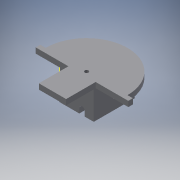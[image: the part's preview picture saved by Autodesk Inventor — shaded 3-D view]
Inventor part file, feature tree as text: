
AUTODESK INVENTOR PART (.ipt)
format: ipt  version: 2016 (Build 200138000, 138)  size: 617,472 bytes
history: native  units: in
note: dims shown in document units (in); Inventor stores cm internally (conversion verified against a paired STEP export)
features: reference x42, extrude x34, sketch x34, plane x6, projected_geometry x5
ambient origin geometry x8: Origin, YZ Plane, XZ Plane, XY Plane, X Axis, Y Axis, Z Axis, Center Point
bodies: Solid1 (feature_tree)
feature tree (121):
  extrude  "Extrusion1"  Depth=3.0in
  extrude  "Extrusion2"  Depth=0.1969in
  extrude  "Extrusion3"  Depth=1.0827in
  extrude  "Extrusion5"  Depth=1.0in TaperAngle=0.0deg
  plane  "Work Plane1"
  extrude  "Extrusion6"  Depth=0.0098in
  extrude  "Extrusion9"  Depth=0.0787in
  extrude  "Extrusion14"  Depth=0.1575in
  extrude  "Extrusion15"  Depth=1.25in
  plane  "Work Plane2"
  extrude  "Extrusion16"  Depth=0.1575in
  extrude  "Extrusion17"  Depth=0.1181in TaperAngle=0.0deg
  extrude  "Extrusion18"  Depth=0.1969in
  plane  "Work Plane3"
  extrude  "Extrusion20"  Depth=0.1969in TaperAngle=0.0deg
  extrude  "Extrusion21"  Depth=0.1181in TaperAngle=0.0deg
  plane  "Work Plane4"
  plane  "Work Plane5"
  extrude  "Extrusion23"  Depth=0.1181in
  extrude  "Extrusion24"  Depth=0.1969in TaperAngle=0.0deg
  plane  "Work Plane6"
  extrude  "Extrusion25"  Depth=0.35in
  extrude  "Extrusion26"  Depth=0.2in
  extrude  "Extrusion27"  Depth=0.1969in TaperAngle=0.0deg
  extrude  "Extrusion28"  Depth=1.5in
  extrude  "Extrusion29"  Depth=0.7in
  extrude  "Extrusion30"  Depth=0.1181in TaperAngle=0.0deg
  extrude  "Extrusion31"  Depth=1.0in
  extrude  "Extrusion34"  Depth=0.5in
  sketch  "Sketch36"  dims[d105=0.1181in d106=0.5in]
  extrude  "Extrusion35"  Depth=0.5in
  extrude  "Extrusion36"  Depth=0.0197in
  extrude  "Extrusion37"  Depth=0.325in
  extrude  "Extrusion38"  Depth=0.1969in
  extrude  "Extrusion39"  Depth=0.1181in
  sketch  "Sketch41"  dims[d117=0.1969in d118=0.1181in]
  extrude  "Extrusion41"  Depth=0.1969in TaperAngle=0.0deg
  extrude  "Extrusion42"  Depth=1.0in TaperAngle=0.0deg
  extrude  "Extrusion43"  Depth=0.5in
  extrude  "Extrusion44"  Depth=0.0039in
  extrude  "Extrusion45"  Depth=0.0984in
  extrude  "Extrusion46"  Depth=0.3937in
  sketch  "Sketch1"  dims[d0=4.5in d1=3.0in]
  sketch  "Sketch2"  dims[d2=0.1969in d3=0.0in d5=0.0787in]
  reference  "Reference1"
  reference  "Reference2"
  sketch  "Sketch3"  dims[d6=1.0in d7=0.0in d8=1.0827in]
  sketch  "Sketch5"  dims[d9=0.3937in d10=1.0in d11=0.0in]
  reference  "Reference14"
  reference  "Reference15"
  reference  "Reference16"
  reference  "Reference17"
  reference  "Reference18"
  sketch  "Sketch6"  dims[d12=0.0787in d23=0.0098in]
  reference  "Reference19"
  sketch  "Sketch9"  dims[d24=0.1575in d25=0.0787in]
  projected_geometry  "Projected Loop2"
  sketch  "Sketch14"  dims[d26=0.0098in d27=0.1575in]
  sketch  "Sketch15"  dims[d28=0.1181in d29=0.0in d30=1.25in]
  sketch  "Sketch16"  dims[d31=0.1575in d32=0.1575in]
  reference  "Reference30"
  sketch  "Sketch17"  dims[d33=0.1181in d34=0.0in d46=0.9201in d47=0.0in]
  reference  "Reference31"
  reference  "Reference32"
  reference  "Reference33"
  reference  "Reference35"
  reference  "Reference36"
  reference  "Reference37"
  reference  "Reference38"
  reference  "Reference39"
  reference  "Reference40"
  reference  "Reference41"
  reference  "Reference42"
  reference  "Reference43"
  reference  "Reference44"
  reference  "Reference45"
  reference  "Reference46"
  reference  "Reference47"
  reference  "Reference48"
  reference  "Reference49"
  sketch  "Sketch20"  dims[d58=0.1969in d59=0.1969in]
  reference  "Reference50"
  sketch  "Sketch21"  dims[d60=0.1969in d61=0.1969in d62=0.0in]
  sketch  "Sketch23"  dims[d63=1.0in d64=0.0in d65=0.1181in d66=0.0in]
  reference  "Reference53"
  reference  "Reference54"
  sketch  "Sketch24"  dims[d67=0.1969in d68=0.0in d69=0.1181in]
  sketch  "Sketch25"  dims[d70=0.1181in d71=0.1969in d72=0.0in]
  reference  "Reference55"
  reference  "Reference56"
  sketch  "Sketch26"  dims[d75=0.0394in d76=0.35in]
  reference  "Reference57"
  reference  "Reference58"
  sketch  "Sketch28"  dims[d77=0.1628in d78=0.2in]
  sketch  "Sketch29"  dims[d79=0.0787in d80=0.0in d81=0.1969in d82=0.0in]
  sketch  "Sketch30"  dims[d89=1.5in d90=1.5in]
  reference  "Reference59"
  sketch  "Sketch31"  dims[d91=0.1181in d92=0.0in d93=0.7in]
  sketch  "Sketch32"  dims[d94=1.26in d95=0.0in d96=0.1181in d97=0.0in]
  sketch  "Sketch35"  dims[d98=0.1181in d99=0.0in d104=1.0in]
  reference  "Reference61"
  sketch  "Sketch37"  dims[d107=1.0in d108=0.5in]
  reference  "Reference62"
  sketch  "Sketch38"  dims[d109=10.0in d110=0.0in d111=0.0197in]
  reference  "Reference63"
  sketch  "Sketch39"  dims[d112=0.0197in d113=0.325in]
  reference  "Reference64"
  sketch  "Sketch40"  dims[d114=0.197in d115=0.0in d116=0.1969in]
  reference  "Reference65"
  projected_geometry  "Projected Loop6"
  sketch  "Sketch42"  dims[d119=0.1969in d120=0.0in d121=0.1575in d122=0.0in]
  projected_geometry  "Projected Loop7"
  sketch  "Sketch43"  dims[d123=0.1in d124=0.0in d132=1.0in d133=0.0in]
  reference  "Reference66"
  sketch  "Sketch44"  dims[d134=0.5in d135=0.5in]
  sketch  "Sketch45"  dims[d136=0.0039in d137=0.0039in]
  projected_geometry  "Projected Loop8"
  projected_geometry  "Projected Loop9"
  sketch  "Sketch46"  dims[d138=0.0984in d139=0.0984in]
  sketch  "Sketch47"  dims[d140=0.0039in d141=0.0984in d142=1.61in d143=0.0in d144=0.2in d145=0.0in d146=0.1181in d147=0.85in d148=0.0in d149=1.2in d150=0.1181in d151=1.1in d152=0.0in d153=0.28in d154=3.0in d155=0.0in d158=222.0in d159=0.0in d160=0.5in d161=1.0in d162=0.2in d163=0.0in d164=0.2in d165=5.0in d166=0.0in d167=0.0394in d168=0.0in d169=0.0394in d170=111.0in d171=0.0in d172=0.1378in d173=0.3937in d174=0.0in]
  reference  "Reference67"
